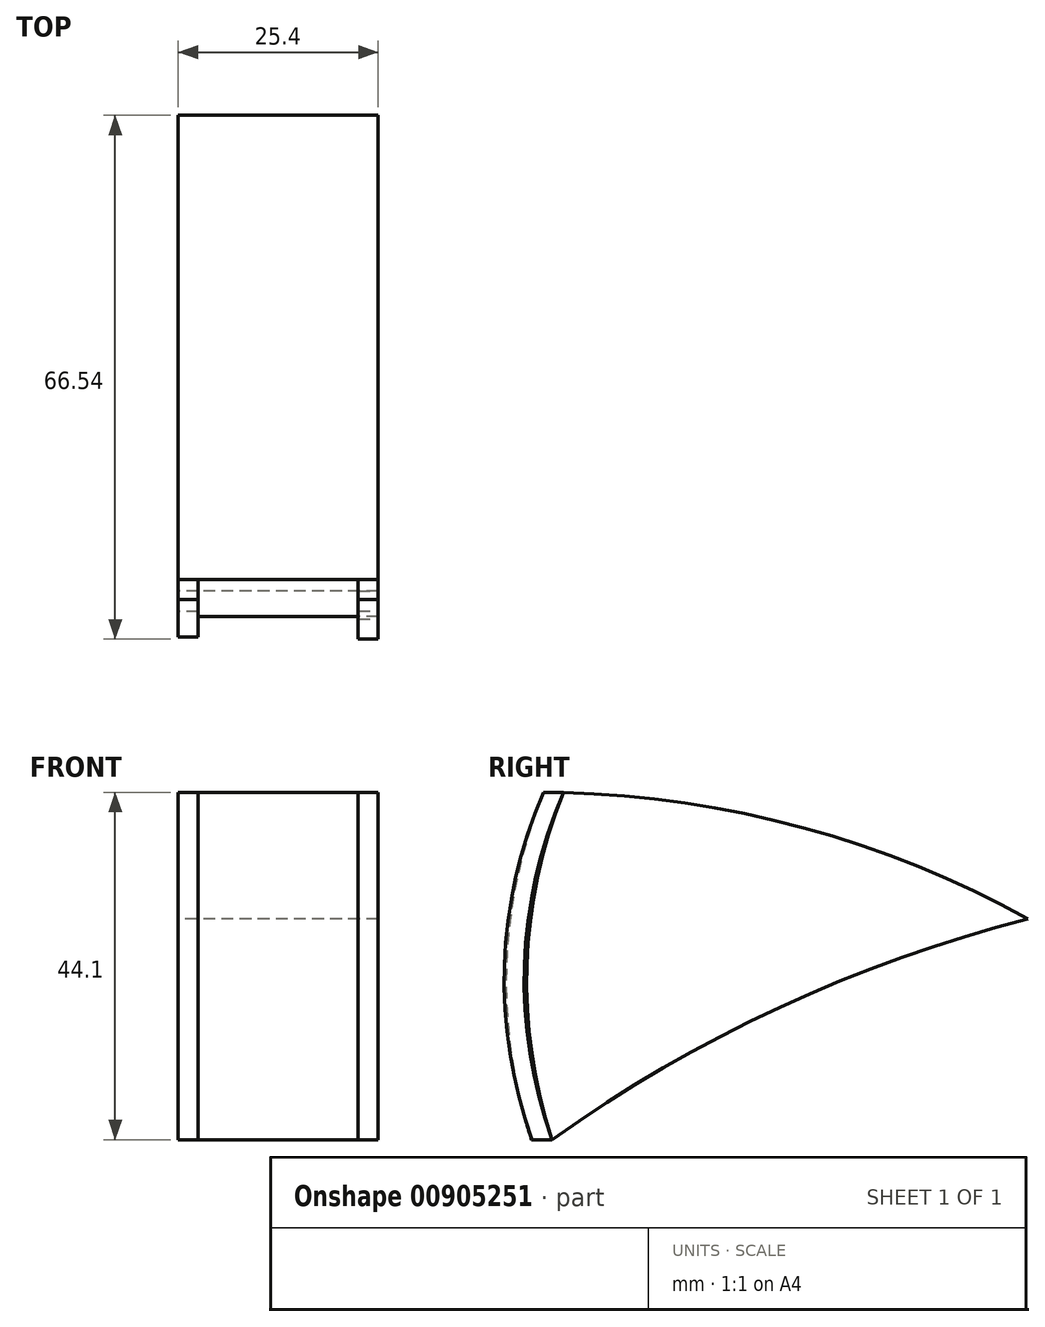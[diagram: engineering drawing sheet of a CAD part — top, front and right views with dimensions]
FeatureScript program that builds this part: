
annotation { "Feature Type Name" : "Feature", "Feature Type Description" : "" }
export const myFeature = defineFeature(function(context is Context, id is Id, definition is map)
    precondition{}
    {
        {
            var Q0;
            Q0=qCreatedBy(makeId("Right.planeOp"),FACE);
            var sketch = newSketch(context, id + "F0", { "sketchPlane" : qUnion([Q0])});
            skArc(sketch, "E0", {"start": v(43.8, 3.07) * mm, "mid": v(12.28, -8.14) * mm, "end": v(-16.64, -24.97) * mm});
            skArc(sketch, "E1", {"start": v(43.8, 3.07) * mm, "mid": v(15.28, 14.65) * mm, "end": v(-15.18, 19.13) * mm});
            skArc(sketch, "E2", {"start": v(-15.18, 19.13) * mm, "mid": v(-19.85, -2.79) * mm, "end": v(-16.64, -24.97) * mm});
            skSolve(sketch);
        }
        {
            var Q0;
            Q0 = qSketchRegion(id + "F0", true);
            extrude(context, id + "F1", {"entities" : qUnion([Q0]), "depth" : 25.4 * mm, "offsetDistance" : 25.4 * mm});
        }
        {
            var Q0;
            Q0=makeQuery(id+"F1.opExtrude","CAP_FACE",FACE,{"disambiguationData":[OSD([sQuery(id+"F0.wireOp",EDGE,"E0"),sQuery(id+"F0.wireOp",EDGE,"E1"),sQuery(id+"F0.wireOp",EDGE,"E2")])],"isStart":false});
            var sketch = newSketch(context, id + "F2", { "sketchPlane" : qUnion([Q0])});
            skArc(sketch, "E3", {"start": v(-15.18, 19.13) * mm, "mid": v(-20.17, -2.78) * mm, "end": v(-16.64, -24.97) * mm});
            skArc(sketch, "E4", {"start": v(-17.72, 19.13) * mm, "mid": v(-22.7, -2.78) * mm, "end": v(-19.18, -24.97) * mm});
            skLineSegment(sketch, "E5", {"start": v(-15.18, 19.13) * mm, "end": v(-17.72, 19.13) * mm});
            skLineSegment(sketch, "E6", {"start": v(-16.64, -24.97) * mm, "end": v(-19.18, -24.97) * mm});
            skSolve(sketch);
        }
        {
            var Q0;
            Q0 = qSketchRegion(id + "F2", true);
            extrude(context, id + "F3", {"entities" : qUnion([Q0]), "oppositeDirection" : true, "depth" : 2.54 * mm, "offsetDistance" : 25.4 * mm});
        }
        {
            var Q0;
            Q0=makeQuery(id+"F1.opExtrude","CAP_FACE",FACE,{"disambiguationData":[OSD([sQuery(id+"F0.wireOp",EDGE,"E0"),sQuery(id+"F0.wireOp",EDGE,"E1"),sQuery(id+"F0.wireOp",EDGE,"E2")])],"isStart":true});
            var sketch = newSketch(context, id + "F4", { "sketchPlane" : qUnion([Q0])});
            skArc(sketch, "E7", {"start": v(16.64, -24.97) * mm, "mid": v(19.83, -2.8) * mm, "end": v(15.18, 19.13) * mm});
            skArc(sketch, "E8", {"start": v(19.25, -24.97) * mm, "mid": v(22.46, -2.78) * mm, "end": v(17.72, 19.13) * mm});
            skPoint(sketch, "E8.startSnap0", {"position": v(19.85, -2.79) * mm});
            skLineSegment(sketch, "E9", {"start": v(19.85, -24.97) * mm, "end": v(16.64, -24.97) * mm});
            skLineSegment(sketch, "E10", {"start": v(17.72, 19.13) * mm, "end": v(15.18, 19.13) * mm});
            skSolve(sketch);
        }
        {
            var Q0;
            Q0 = qSketchRegion(id + "F4", true);
            extrude(context, id + "F5", {"entities" : qUnion([Q0]), "operationType" : NewBodyOperationType.ADD, "oppositeDirection" : true, "depth" : 2.54 * mm, "offsetDistance" : 25.4 * mm});
        }
    });
